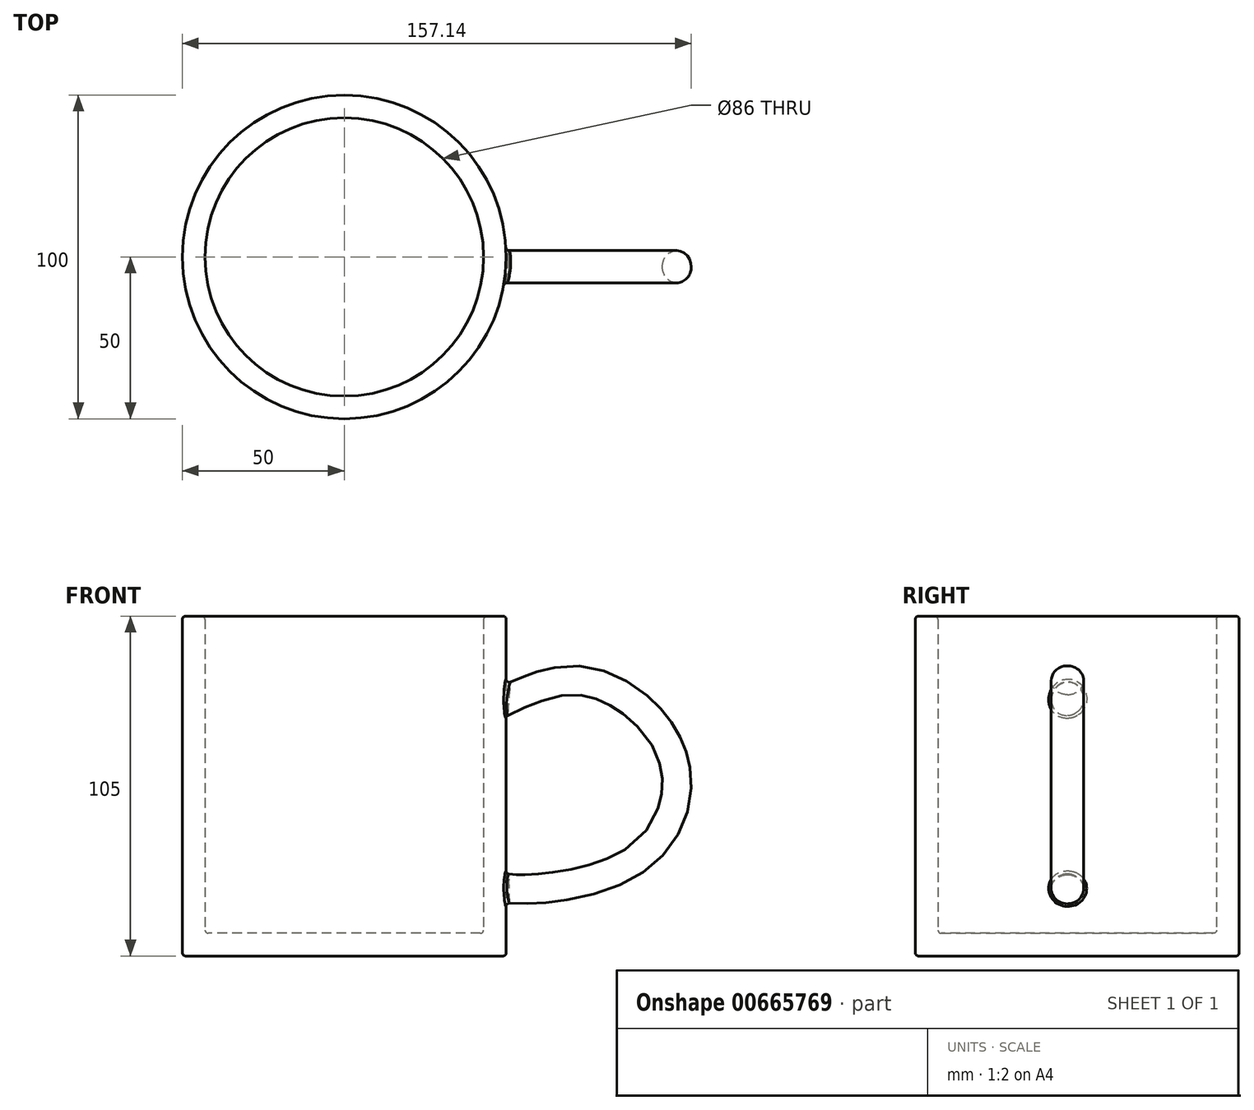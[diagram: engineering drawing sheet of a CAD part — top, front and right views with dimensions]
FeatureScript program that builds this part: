
annotation { "Feature Type Name" : "Feature", "Feature Type Description" : "" }
export const myFeature = defineFeature(function(context is Context, id is Id, definition is map)
    precondition{}
    {
        {
            var Q0;
            Q0=qCreatedBy(makeId("Top.planeOp"),FACE);
            var sketch = newSketch(context, id + "F0", { "sketchPlane" : qUnion([Q0])});
            skCircle(sketch, "E0", {"center": v(0, 0) * mm, "radius": 50 * mm});
            skSolve(sketch);
        }
        {
            var Q0;
            Q0 = qSketchRegion(id + "F0", true);
            extrude(context, id + "F1", {"entities" : qUnion([Q0]), "depth" : 105 * mm, "offsetDistance" : 25 * mm});
        }
        {
            var Q0;
            Q0=qCreatedBy(makeId("Right.planeOp"),FACE);
            cPlane(context, id + "F2", {"entities" : qUnion([Q0]), "cplaneType" : CPlaneType.OFFSET, "offset" : 50 * mm, "width" : 150 * mm, "height" : 150 * mm});
        }
        {
            var Q0;
            Q0=qCreatedBy(makeId("Front.planeOp"),FACE);
            var sketch = newSketch(context, id + "F3", { "sketchPlane" : qUnion([Q0])});
            skFitSpline(sketch, "E1", {"points": [v(45.9, 78.26) * mm, v(75.44, 85.7) * mm, v(102.28, 62.02) * mm, v(92.36, 30.22) * mm, v(55.82, 19.62) * mm, v(45.9, 20.53) * mm], "startDerivative": vector(139.26, 67.87) * mm, "endDerivative": vector(-66.25, 12.29) * mm});
            skSolve(sketch);
        }
        {
            var Q0;
            Q0=qCreatedBy(id+"F2.planeOp",FACE);
            var sketch = newSketch(context, id + "F4", { "sketchPlane" : qUnion([Q0])});
            skCircle(sketch, "E2", {"center": v(-3.03, 79.07) * mm, "radius": 5 * mm});
            skSolve(sketch);
        }
        {
            var Q0;
            Q0=makeQuery(id+"F4.imprint","IMPRINT",FACE,{"disambiguationData":[TD([[makeQuery(id+"F4.imprint","IMPRINT",EDGE,{"derivedFrom":sQuery(id+"F4.wireOp",EDGE,"E2")}),1.0]])]});
            var Q1;
            Q1=sQuery(id+"F3.wireOp",EDGE,"E1");
            sweep(context, id + "F5", {"operationType" : NewBodyOperationType.ADD, "profiles" : qUnion([Q0]), "path" : qUnion([Q1])});
        }
        {
            var Q0;
            Q0=makeQuery(id+"F1.opExtrude","CAP_FACE",FACE,{"disambiguationData":[OSD([sQuery(id+"F0.wireOp",EDGE,"E0")])],"isStart":false});
            shell(context, id + "F6", {"entities" : qUnion([Q0]), "thickness" : 7 * mm});
        }
        {
            var Q0;
            Q0=makeQuery(id+"F1.opExtrude","CAP_FACE",FACE,{"disambiguationData":[OSD([sQuery(id+"F0.wireOp",EDGE,"E0")])],"isStart":false});
            var Q1;
            Q1=makeQuery(id+"F1.opExtrude","CAP_EDGE",EDGE,{"disambiguationData":[OSD([sQuery(id+"F0.wireOp",EDGE,"E0")])],"isStart":false});
            var Q2;
            Q2=makeQuery(id+"F5.boolean.opBoolean","INTERSECT",EDGE,{"disambiguationData":[OD(1.0)],"derivedFrom":[makeQuery(id+"F1.opExtrude","SWEPT_FACE",FACE,{"disambiguationData":[OSD([sQuery(id+"F0.wireOp",EDGE,"E0")])]}),makeQuery(id+"F5.opSweep","SWEPT_FACE",FACE,{"disambiguationData":[OSD([sQuery(id+"F3.wireOp",EDGE,"E1"),sQuery(id+"F4.wireOp",EDGE,"E2")])]})]});
            var Q3;
            Q3=makeQuery(id+"F5.boolean.opBoolean","INTERSECT",EDGE,{"disambiguationData":[OD(0.0)],"derivedFrom":[makeQuery(id+"F1.opExtrude","SWEPT_FACE",FACE,{"disambiguationData":[OSD([sQuery(id+"F0.wireOp",EDGE,"E0")])]}),makeQuery(id+"F5.opSweep","SWEPT_FACE",FACE,{"disambiguationData":[OSD([sQuery(id+"F3.wireOp",EDGE,"E1"),sQuery(id+"F4.wireOp",EDGE,"E2")])]})]});
            var Q4;
            Q4=makeQuery(id+"F1.opExtrude","CAP_EDGE",EDGE,{"disambiguationData":[OSD([sQuery(id+"F0.wireOp",EDGE,"E0")])],"isStart":true});
            var Q5;
            {var subQ0=sQuery(id+"F0.wireOp",EDGE,"E0");Q5=makeQuery(id+"F6.opShell","OFFSET_EDGE",EDGE,{"disambiguationData":[OSD([subQ0]),TDD([makeQuery(id+"F1.opExtrude","CAP_EDGE",EDGE,{"disambiguationData":[OSD([subQ0])],"isStart":true})])]});}
            fillet(context, id + "F7", {"entities" : qUnion([Q0, Q1, Q2, Q3, Q4, Q5]), "radius" : 1 * mm, "tangentPropagation" : true, "allowEdgeOverflow" : false});
        }
    });
